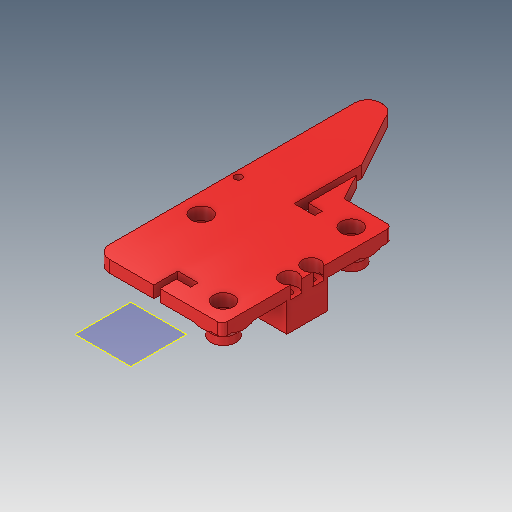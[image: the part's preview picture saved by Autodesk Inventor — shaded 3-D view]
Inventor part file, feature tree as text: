
AUTODESK INVENTOR PART (.ipt)
format: ipt  version: 2019.4 (Build 234330000, 330)  size: 380,928 bytes
history: native  units: mm
features: extrude x9, sketch x8, plane x5, projected_geometry x3, mirror x1, chamfer x1, fillet x1
ambient origin geometry x8: Origin, YZ Plane, XZ Plane, XY Plane, X Axis, Y Axis, Z Axis, Center Point
bodies: Solid1 (feature_tree)
feature tree (28):
  extrude  "Extrusion1"  Depth=9.0mm
  mirror  "Mirror1"
  extrude  "Extrusion2"  Depth=12.0mm
  chamfer  "Chamfer1"  Distance=5.25mm
  extrude  "Extrusion4"  Depth=4.7mm TaperAngle=0.0deg
  extrude  "Extrusion5"  Depth=10.0mm
  fillet  "Fillet1"  Radius=10.0mm
  plane  "Work Plane2"
  plane  "Work Plane6"
  extrude  "Extrusion6"  Depth=10.0mm
  plane  "Work Plane3"
  plane  "Work Plane4"
  extrude  "Extrusion11"  Depth=10.0mm TaperAngle=0.0deg
  extrude  "Extrusion12"  Depth=2.0mm TaperAngle=45.0deg
  extrude  "Extrusion13"  Depth=2.0mm
  plane  "Work Plane5"
  extrude  "Extrusion14"  Depth=8.0mm
  sketch  "Sketch1"  dims[d0=12.5mm d1=20.0mm d2=9.0mm]
  sketch  "Sketch2"  dims[d3=8.7mm d4=12.0mm]
  sketch  "Sketch4"  dims[d5=20.9mm]
  sketch  "Sketch5"  dims[d10=2.8mm]
  projected_geometry  "Projected Loop1"
  sketch  "Sketch11"  dims[d11=4.9mm]
  sketch  "Sketch13"  dims[d12=4.9mm]
  sketch  "Sketch14"  dims[d14=7.8mm]
  projected_geometry  "Projected Loop2"
  sketch  "Sketch15"  dims[d15=8.3mm d19=5.25mm d20=4.7mm d21=0.0mm d22=34.0mm d23=10.0mm d24=10.0mm d26=7.0mm d27=0.0mm d37=4.0mm d38=2.0mm d39=45.0deg d40=2.0mm d41=8.0mm d42=8.0mm d43=8.0mm d44=5.0mm d45=0.0mm d46=5.9mm d47=5.9mm d51=7.0mm d52=0.0mm d53=5.0mm d54=10.0mm d58=15.0mm d60=12.5mm d61=0.0mm d67=16.0mm d68=14.0mm d69=0.0mm d75=7.0mm d76=0.0mm d77=0.0mm d78=3.0mm d79=3.0mm d80=7.0mm d81=7.0mm d82=5.0mm d83=0.0mm d84=2.9mm d85=5.0mm d86=0.0mm d88=25.0mm d90=92.0mm d91=90.0deg d92=90.0deg d93=10.0mm d94=0.0mm d95=2.8mm]
  projected_geometry  "Projected Loop3"
